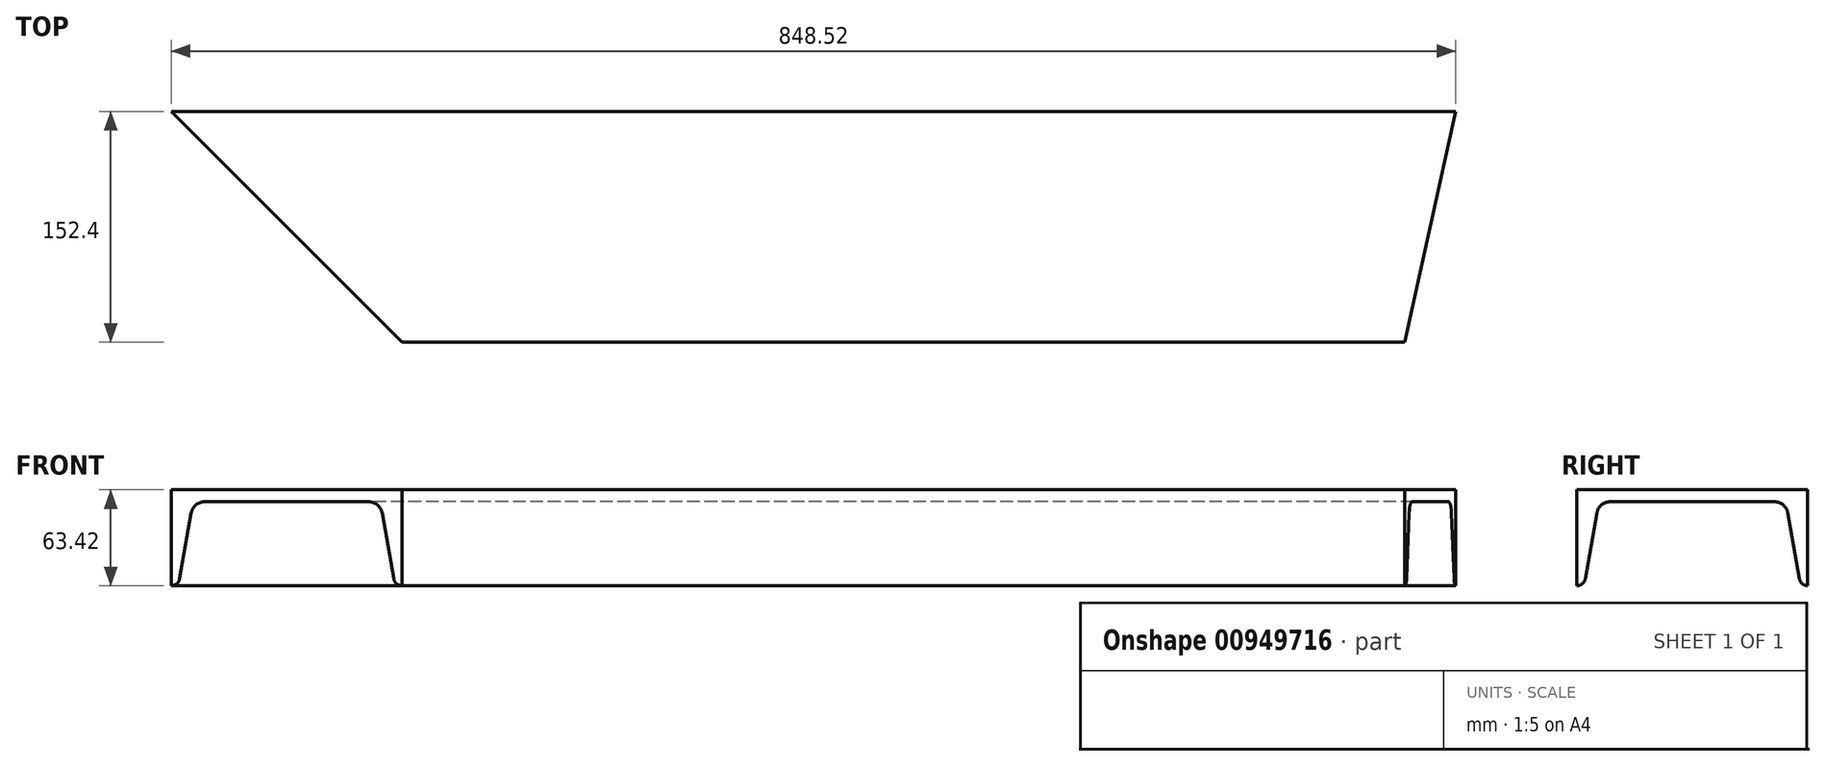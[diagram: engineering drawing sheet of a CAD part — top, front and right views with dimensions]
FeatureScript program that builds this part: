
annotation { "Feature Type Name" : "Feature", "Feature Type Description" : "" }
export const myFeature = defineFeature(function(context is Context, id is Id, definition is map)
    precondition{}
    {
        {
            var Q0;
            Q0=qCreatedBy(makeId("Right.planeOp"),FACE);
            var sketch = newSketch(context, id + "F0", { "sketchPlane" : qUnion([Q0])});
            skLineSegment(sketch, "E0", {"start": v(-76.2, 0) * mm, "end": v(76.2, 0) * mm});
            skLineSegment(sketch, "E1", {"start": v(76.2, 0) * mm, "end": v(76.2, -63.42) * mm});
            skLineSegment(sketch, "E2", {"start": v(-76.2, 0) * mm, "end": v(-76.2, -63.42) * mm});
            skLineSegment(sketch, "E3", {"start": v(-63.12, -15.57) * mm, "end": v(-70.65, -58.76) * mm});
            skLineSegment(sketch, "E4", {"start": v(63.12, -15.57) * mm, "end": v(70.65, -58.76) * mm});
            skLineSegment(sketch, "E5", {"start": v(-53.98, -7.87) * mm, "end": v(53.98, -7.87) * mm});
            skArc(sketch, "E6.filletArc", {"start": v(-76.2, -63.42) * mm, "mid": v(-72.57, -62.1) * mm, "end": v(-70.65, -58.76) * mm});
            skArc(sketch, "E7.filletArc", {"start": v(70.65, -58.76) * mm, "mid": v(72.57, -62.1) * mm, "end": v(76.2, -63.42) * mm});
            skArc(sketch, "E8.filletArc", {"start": v(-53.98, -7.87) * mm, "mid": v(-59.95, -10.05) * mm, "end": v(-63.12, -15.57) * mm});
            skArc(sketch, "E9.filletArc", {"start": v(63.12, -15.57) * mm, "mid": v(59.95, -10.05) * mm, "end": v(53.98, -7.87) * mm});
            skSolve(sketch);
        }
        {
            var Q0;
            Q0=qSketchRegion(id+"F0",true);
            extrude(context, id + "F1", {"entities" : qUnion([Q0]), "depth" : 848.52 * mm, "offsetDistance" : 25.4 * mm});
        }
        {
            var Q0;
            Q0=makeQuery(id+"F1.opExtrude","SWEPT_FACE",FACE,{"disambiguationData":[OSD([sQuery(id+"F0.wireOp",EDGE,"E0")])]});
            var sketch = newSketch(context, id + "F2", { "sketchPlane" : qUnion([Q0])});
            skLineSegment(sketch, "E10", {"start": v(0, 76.2) * mm, "end": v(152.4, -76.2) * mm});
            skLineSegment(sketch, "E11", {"start": v(152.4, -76.2) * mm, "end": v(0, -76.2) * mm});
            skLineSegment(sketch, "E12", {"start": v(0, -76.2) * mm, "end": v(0, 76.2) * mm});
            skLineSegment(sketch, "E13", {"start": v(848.52, 76.2) * mm, "end": v(848.52, -76.2) * mm});
            skLineSegment(sketch, "E14", {"start": v(848.52, -76.2) * mm, "end": v(814.73, -76.2) * mm});
            skLineSegment(sketch, "E15", {"start": v(814.73, -76.2) * mm, "end": v(848.52, 76.2) * mm});
            skSolve(sketch);
        }
        {
            var Q0;
            Q0=qSketchRegion(id+"F2",true);
            extrude(context, id + "F3", {"entities" : qUnion([Q0]), "operationType" : NewBodyOperationType.REMOVE, "endBound" : BoundingType.THROUGH_ALL, "oppositeDirection" : true, "depth" : 25.4 * mm, "offsetDistance" : 25.4 * mm});
        }
    });
